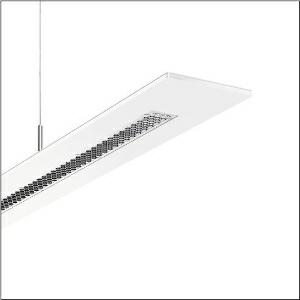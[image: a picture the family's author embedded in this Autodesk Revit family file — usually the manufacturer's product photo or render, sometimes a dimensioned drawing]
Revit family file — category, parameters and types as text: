
# Revit family: arktika_r__21_5mb2512l30840_559e
name_source: partatom
category: Lighting Fixtures
units: mm (PartAtom-declared; Revit-internal decimal feet)

## family parameters
Cut with Voids When Loaded = No
Host = Face
Light Source = No
Part Type = Normal
Room Calculation Point = No
Round Connector Dimension = Use Diameter
Shared = No

## types (1)
- Arktika® 21 (1 x LED 4000K / CRI = 80 (unbekannt), 4000 lm, 4000K)
    Apparent Load = 31 VA
    CIE Flux Codes = 81 100 100 79 100
    Color Rendering = 80
    Color Temperature = 4000K
    Default Elevation = 1800 mm
    Description = Arktika® 21, office luminaire, primary anti-glare with honeycomb louvre, of plastic, aluminium vaporised, highly specular, light emission: direct/indirect distribution, primary light characteristic: symmetric, installation type: suspended mounting, LED, rated luminous flux: 4.000lm, luminous efficacy: 130lm/W, light colour: 840, colour temperature: 4000K, control gear: ON/OFF, with terminal, 3-pole, mains connection: 220..240V, AC, 50/60Hz, rated input power: 31W, housing, of aluminium, powder-coated, traffic white (RAL 9016), 1-length, length: 1.250mm, width: 120mm, height: 8mm, protection rating (complete): IP20, insulation class (complete): insulation class II (safety insulation), certification: CE, packaging unit: 1 piece
    Height = 8 mm  [stored 0.0262467 ft]
    Lamp = 1 x LED 4000K / CRI >= 80 (unbekannt)
    Lamp Light Flux = 4000 lm
    Lamp count = 1
    Length = 1250 mm
    Luminous efficacy = 130 lm/W
    Manufacturer = Siteco
    ModVariant = No
    Model = 5MB2512L30840
    Mounting Place = Ceiling
    Mounting Type = Pendant
    Number of Poles = 1
    OnlyDefault = Yes
    Power Factor = 1
    Product Name = Arktika® 21
    Product group = office luminaire | ceiling pendant
    ProductGroupID = 904
    Protection Class = Protection class II
    Protection Degree = IP 20
    RLX_Detail_Level = 1
    RLX_Emergency_Light_Flux = 0 lm
    RLX_Emergency_Type = 0
    RLX_Emergency_Type_DB = No
    RlxData = <blob elided: 36109 chars, md5=e67735fa>
    Socket = socket
    Standby Power = 0 W
    System Light Flux = 4000 lm
    System Power = 31 W
    Type Comments = Product without accessories
    Type Image = l_1006128.jpg
    URL = http://relux.com
    VarID = ---
    Voltage = 0 V
    Weight = 0.00 kg
    Width = 120 mm

note: [stored X ft] marks values corroborated as IEEE doubles in the binary element streams (Revit-internal decimal feet)

## geometry (parser evidence)
native form markers: Blend x4, Sweep x11
no freeform markers — native parametric forms only
